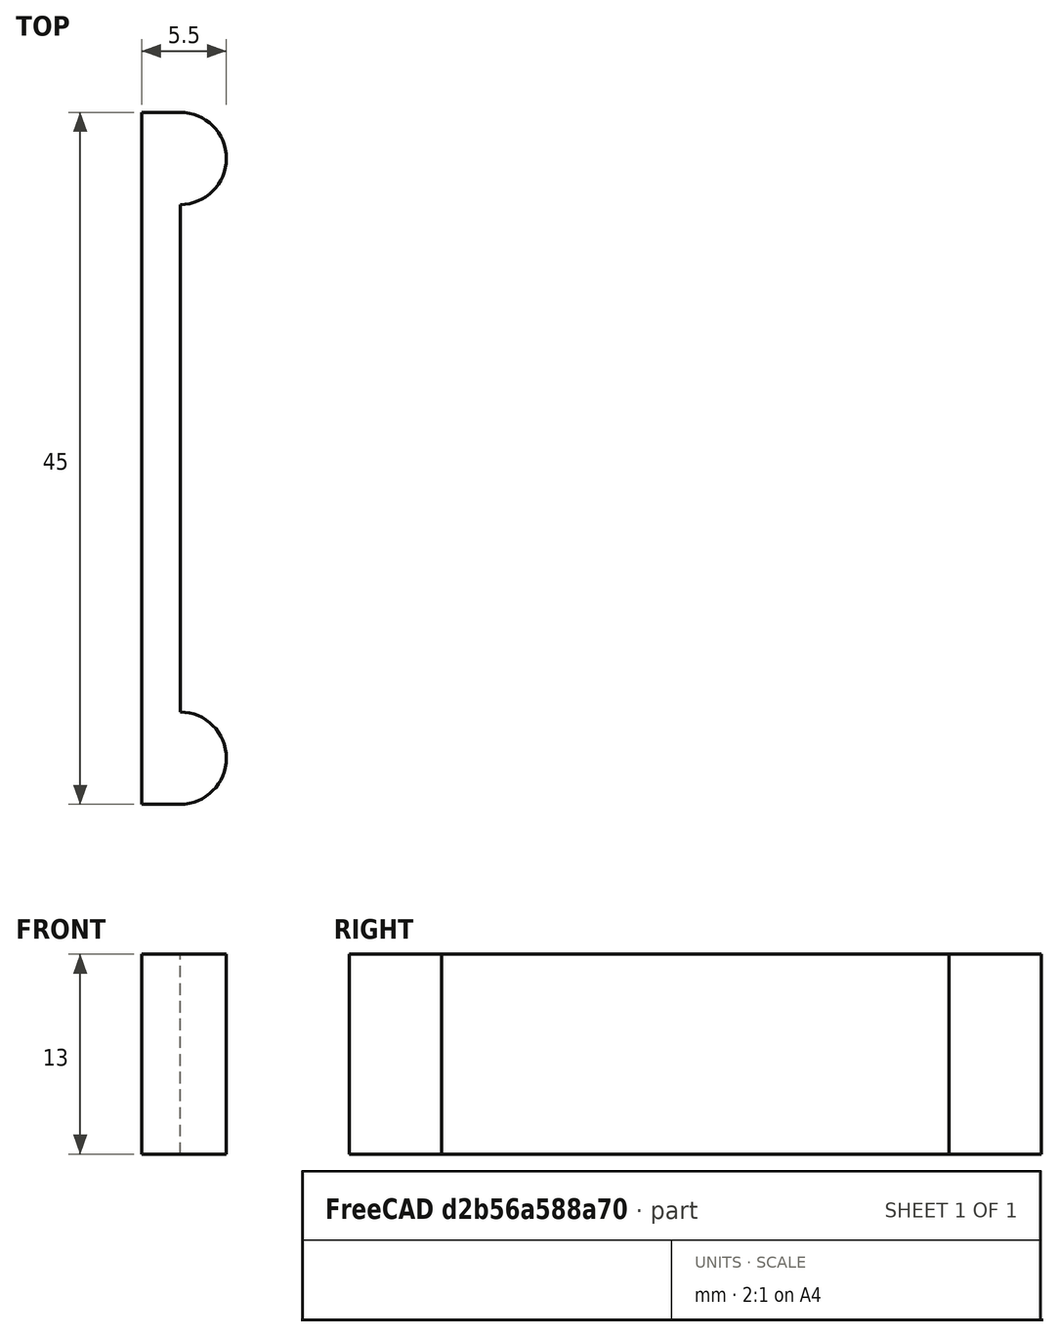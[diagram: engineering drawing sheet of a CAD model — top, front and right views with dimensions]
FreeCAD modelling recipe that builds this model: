
FCSTD DOCUMENT  (FreeCAD 0.22R37573 (Git))
Label: tiny lavalier mic clip
License: All rights reserved
LicenseURL: http://en.wikipedia.org/wiki/All_rights_reserved
objects: Sketcher::SketchObject×1, PartDesign::Pad×1, PartDesign::Body×1
note: 4 computed .brp shape members not serialized (recipe doc carries the construction recipe); baked Part::Feature solids carry a one-line shape summary decoded from their .brp

FEATURE [Sketcher::SketchObject] Sketch
  AttachmentSupport = -> [XY_Plane]
  FullyConstrained = true
  MapMode = 5
  Support = -> [XY_Plane]
  sketch-geometry (6):
    g0: LineSegment StartX=0 StartY=0 StartZ=0 EndX=0 EndY=45 EndZ=0
    g1: LineSegment StartX=0 StartY=45 StartZ=0 EndX=2.5 EndY=45 EndZ=0
    g2: LineSegment StartX=0 StartY=0 StartZ=0 EndX=2.5 EndY=0 EndZ=0
    g3: LineSegment StartX=2.5 StartY=39 StartZ=0 EndX=2.5 EndY=6 EndZ=0
    g4: ArcOfCircle CenterX=2.5 CenterY=42 CenterZ=0 NormalX=0 NormalY=0 NormalZ=1 AngleXU=0 Radius=3 StartAngle=4.71239 EndAngle=7.85398
    g5: ArcOfCircle CenterX=2.5 CenterY=3 CenterZ=0 NormalX=0 NormalY=0 NormalZ=1 AngleXU=0 Radius=3 StartAngle=4.71239 EndAngle=7.85398
  constraints (17):
    c: Coincident(g1,g0)
    c: Horizontal(g1)
    c: Coincident(g2,g0)
    c: Horizontal(g2)
    c: Vertical(g3)
    c: Coincident(g4,g3)
    c: Tangent(g5,g2) = -1.5708
    c: Tangent(g4,g1) = 1.5708
    c: Vertical(g1,g3)
    c: PointOnObject(g0,g-2)
    c: Coincident(g0,g-1)
    c: DistanceX(g1,g1) = 2.5
    c: Coincident(g3,g5)
    c: Perpendicular(g5,g3)
    c: Equal(g4,g5)
    c: DistanceY(g0,g0) = 45
    c: Radius(g4) = 3
FEATURE [PartDesign::Pad] Pad
  Direction = (0,0,1)
  Length = 13
  Length2 = 10
  Profile = -> Sketch
  ReferenceAxis = -> Sketch [N_Axis]
  Suppressed = false
  Type = 0
FEATURE [PartDesign::Body] Body
  AllowCompound = false
  Group = -> [Sketch,Pad]
  Origin = -> Origin
  Tip = -> Pad
